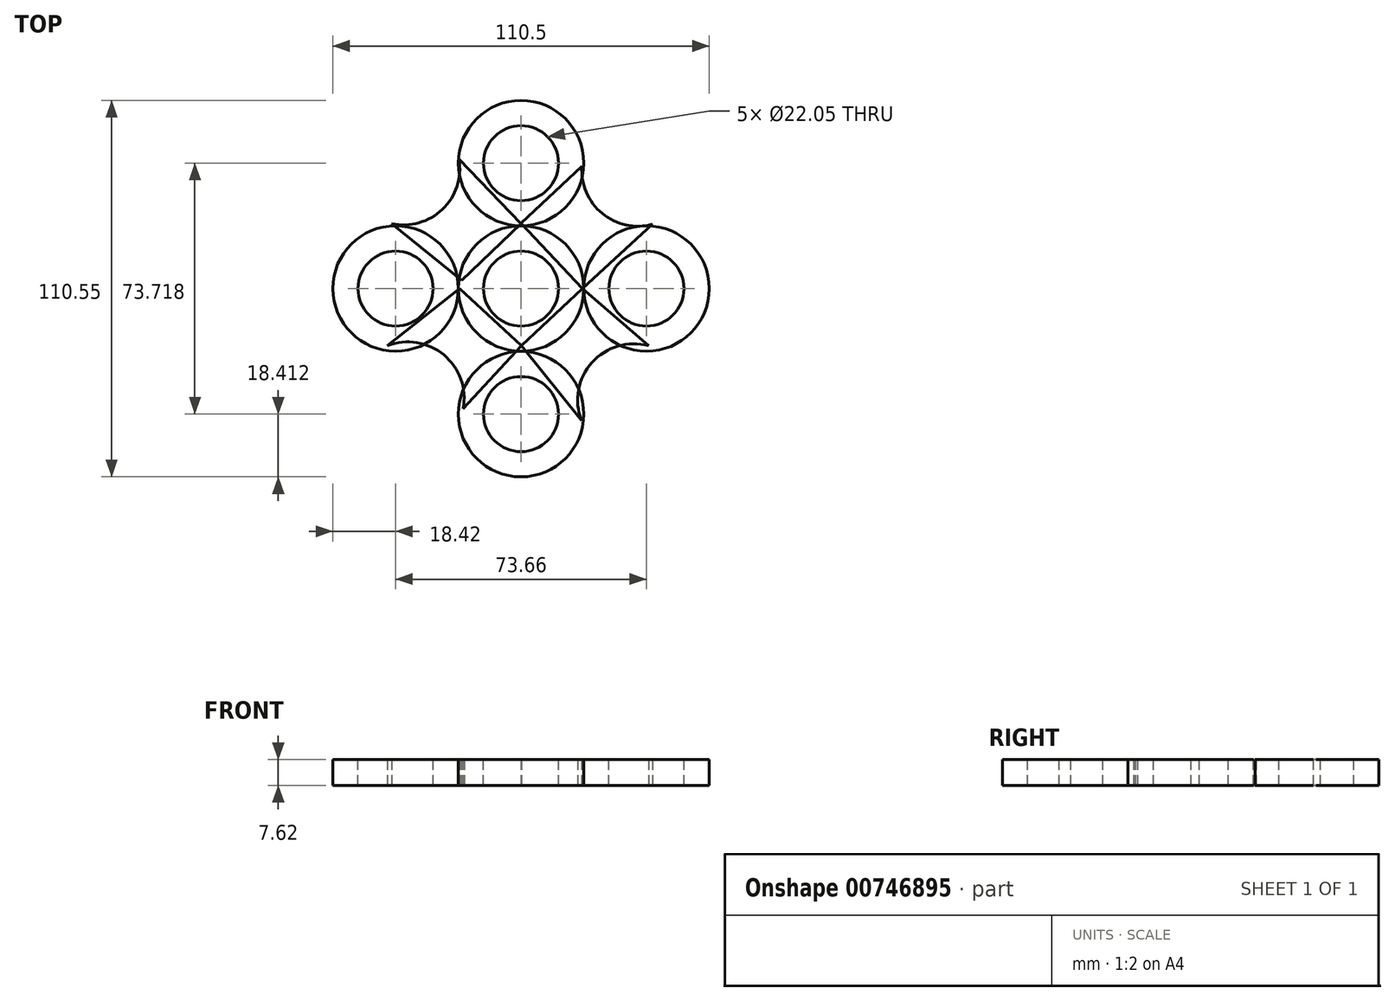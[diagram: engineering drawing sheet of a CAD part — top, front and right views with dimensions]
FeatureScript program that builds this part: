
annotation { "Feature Type Name" : "Feature", "Feature Type Description" : "" }
export const myFeature = defineFeature(function(context is Context, id is Id, definition is map)
    precondition{}
    {
        {
            var Q0;
            Q0=qCreatedBy(makeId("Top.planeOp"),FACE);
            var sketch = newSketch(context, id + "F0", { "sketchPlane" : qUnion([Q0])});
            skCircle(sketch, "E0", {"center": v(0, 0) * mm, "radius": 18.41 * mm});
            skSolve(sketch);
        }
        {
            var Q0;
            Q0=makeQuery(id+"F0.imprint","IMPRINT",FACE,{"disambiguationData":[TD([[makeQuery(id+"F0.imprint","IMPRINT",EDGE,{"derivedFrom":sQuery(id+"F0.wireOp",EDGE,"E0")}),1.0]])]});
            extrude(context, id + "F1", {"entities" : qUnion([Q0]), "depth" : 7.62 * mm, "offsetDistance" : 25.4 * mm});
        }
        {
            var Q0;
            Q0=makeQuery(id+"F1.opExtrude","CAP_FACE",FACE,{"disambiguationData":[OSD([sQuery(id+"F0.wireOp",EDGE,"E0")])],"isStart":false});
            var sketch = newSketch(context, id + "F2", { "sketchPlane" : qUnion([Q0])});
            skCircle(sketch, "E1", {"center": v(0, 0) * mm, "radius": 11.02 * mm});
            skSolve(sketch);
        }
        {
            var Q0;
            Q0 = qSketchRegion(id + "F2", true);
            extrude(context, id + "F3", {"entities" : qUnion([Q0]), "operationType" : NewBodyOperationType.REMOVE, "oppositeDirection" : true, "depth" : 25.4 * mm, "offsetDistance" : 25.4 * mm});
        }
        {
            var Q0;
            Q0=qCreatedBy(makeId("Top.planeOp"),FACE);
            var sketch = newSketch(context, id + "F4", { "sketchPlane" : qUnion([Q0])});
            skCircle(sketch, "E2", {"center": v(0, 36.83) * mm, "radius": 18.41 * mm});
            skSolve(sketch);
        }
        {
            var Q0;
            Q0 = qSketchRegion(id + "F4", true);
            extrude(context, id + "F5", {"entities" : qUnion([Q0]), "operationType" : NewBodyOperationType.ADD, "depth" : 7.62 * mm, "offsetDistance" : 25.4 * mm});
        }
        {
            var Q0;
            Q0=qCreatedBy(makeId("Top.planeOp"),FACE);
            var sketch = newSketch(context, id + "F6", { "sketchPlane" : qUnion([Q0])});
            skCircle(sketch, "E3", {"center": v(-36.83, 0) * mm, "radius": 18.41 * mm});
            skCircle(sketch, "E4", {"center": v(36.83, 0) * mm, "radius": 18.41 * mm});
            skCircle(sketch, "E5", {"center": v(0, -36.89) * mm, "radius": 18.41 * mm});
            skSolve(sketch);
        }
        {
            var Q0;
            Q0 = qSketchRegion(id + "F6", true);
            extrude(context, id + "F7", {"entities" : qUnion([Q0]), "operationType" : NewBodyOperationType.ADD, "depth" : 7.62 * mm, "offsetDistance" : 25.4 * mm});
        }
        {
            var Q0;
            Q0=qCreatedBy(makeId("Top.planeOp"),FACE);
            var sketch = newSketch(context, id + "F8", { "sketchPlane" : qUnion([Q0])});
            skArc(sketch, "E6", {"start": v(-37.97, 19.07) * mm, "mid": v(-23.08, 23.27) * mm, "end": v(-18.21, 37.97) * mm});
            skLineSegment(sketch, "E7", {"start": v(-37.97, 19.07) * mm, "end": v(-17.45, 2.41) * mm});
            skLineSegment(sketch, "E8", {"start": v(-17.45, 2.41) * mm, "end": v(0, 19.07) * mm});
            skLineSegment(sketch, "E9", {"start": v(0, 19.07) * mm, "end": v(-18.21, 37.97) * mm});
            skSolve(sketch);
        }
        {
            var Q0;
            Q0 = qSketchRegion(id + "F8", true);
            extrude(context, id + "F9", {"entities" : qUnion([Q0]), "depth" : 7.62 * mm, "offsetDistance" : 25.4 * mm});
        }
        {
            var Q0;
            Q0=qCreatedBy(makeId("Top.planeOp"),FACE);
            var sketch = newSketch(context, id + "F10", { "sketchPlane" : qUnion([Q0])});
            skArc(sketch, "E10", {"start": v(17.86, 35.94) * mm, "mid": v(23.84, 22.06) * mm, "end": v(38.6, 18.86) * mm});
            skLineSegment(sketch, "E11", {"start": v(17.86, 35.94) * mm, "end": v(0, 19.15) * mm});
            skLineSegment(sketch, "E12", {"start": v(0, 19.15) * mm, "end": v(18, 0) * mm});
            skLineSegment(sketch, "E13", {"start": v(18, 0) * mm, "end": v(38.6, 18.86) * mm});
            skArc(sketch, "E14", {"start": v(37.43, -16.82) * mm, "mid": v(20.85, -21.71) * mm, "end": v(17.72, -38.71) * mm});
            skArc(sketch, "E15", {"start": v(-17, -35.29) * mm, "mid": v(-22.65, -19.49) * mm, "end": v(-39.2, -16.79) * mm});
            skLineSegment(sketch, "E16", {"start": v(37.43, -16.82) * mm, "end": v(18, 0) * mm});
            skLineSegment(sketch, "E17", {"start": v(18, 0) * mm, "end": v(0.1, -16.82) * mm});
            skLineSegment(sketch, "E18", {"start": v(0.1, -16.82) * mm, "end": v(17.72, -38.71) * mm});
            skLineSegment(sketch, "E19", {"start": v(-17, -35.29) * mm, "end": v(0.1, -16.82) * mm});
            skLineSegment(sketch, "E20", {"start": v(0.1, -16.82) * mm, "end": v(-18.05, 0) * mm});
            skLineSegment(sketch, "E21", {"start": v(-18.05, 0) * mm, "end": v(-39.2, -16.79) * mm});
            skSolve(sketch);
        }
        {
            var Q0;
            Q0 = qSketchRegion(id + "F10", true);
            extrude(context, id + "F11", {"entities" : qUnion([Q0]), "depth" : 7.62 * mm, "offsetDistance" : 25.4 * mm});
        }
        {
            var Q0;
            Q0=makeQuery(id+"F5.opExtrude","CAP_FACE",FACE,{"disambiguationData":[OSD([sQuery(id+"F4.wireOp",EDGE,"E2")])],"isStart":false});
            var sketch = newSketch(context, id + "F12", { "sketchPlane" : qUnion([Q0])});
            skCircle(sketch, "E22", {"center": v(0, 36.83) * mm, "radius": 11.02 * mm});
            skSolve(sketch);
        }
        {
            var Q0;
            Q0=makeQuery(id+"F12.imprint","IMPRINT",FACE,{"disambiguationData":[TD([[makeQuery(id+"F12.imprint","IMPRINT",EDGE,{"derivedFrom":sQuery(id+"F12.wireOp",EDGE,"E22")}),1.0]])]});
            extrude(context, id + "F13", {"entities" : qUnion([Q0]), "operationType" : NewBodyOperationType.REMOVE, "oppositeDirection" : true, "depth" : 25.4 * mm, "offsetDistance" : 25.4 * mm});
        }
        {
            var Q0;
            Q0=makeQuery(id+"F7.opExtrude","CAP_FACE",FACE,{"disambiguationData":[OSD([sQuery(id+"F6.wireOp",EDGE,"E3")])],"isStart":false});
            var sketch = newSketch(context, id + "F14", { "sketchPlane" : qUnion([Q0])});
            skCircle(sketch, "E23", {"center": v(-36.83, 0) * mm, "radius": 11.02 * mm});
            skSolve(sketch);
        }
        {
            var Q0;
            Q0 = qSketchRegion(id + "F14", true);
            extrude(context, id + "F15", {"entities" : qUnion([Q0]), "operationType" : NewBodyOperationType.REMOVE, "oppositeDirection" : true, "depth" : 25.4 * mm, "offsetDistance" : 25.4 * mm});
        }
        {
            var Q0;
            Q0=makeQuery(id+"F7.opExtrude","CAP_FACE",FACE,{"disambiguationData":[OSD([sQuery(id+"F6.wireOp",EDGE,"E5")])],"isStart":false});
            var sketch = newSketch(context, id + "F16", { "sketchPlane" : qUnion([Q0])});
            skCircle(sketch, "E24", {"center": v(0, -36.89) * mm, "radius": 11.02 * mm});
            skSolve(sketch);
        }
        {
            var Q0;
            Q0 = qSketchRegion(id + "F16", true);
            extrude(context, id + "F17", {"entities" : qUnion([Q0]), "operationType" : NewBodyOperationType.REMOVE, "oppositeDirection" : true, "depth" : 25.4 * mm, "offsetDistance" : 25.4 * mm});
        }
        {
            var Q0;
            Q0=makeQuery(id+"F7.opExtrude","CAP_FACE",FACE,{"disambiguationData":[OSD([sQuery(id+"F6.wireOp",EDGE,"E4")])],"isStart":false});
            var sketch = newSketch(context, id + "F18", { "sketchPlane" : qUnion([Q0])});
            skCircle(sketch, "E25", {"center": v(36.83, 0) * mm, "radius": 11.02 * mm});
            skSolve(sketch);
        }
        {
            var Q0;
            Q0 = qSketchRegion(id + "F18", true);
            extrude(context, id + "F19", {"entities" : qUnion([Q0]), "operationType" : NewBodyOperationType.REMOVE, "oppositeDirection" : true, "depth" : 25.4 * mm, "offsetDistance" : 25.4 * mm});
        }
    });
